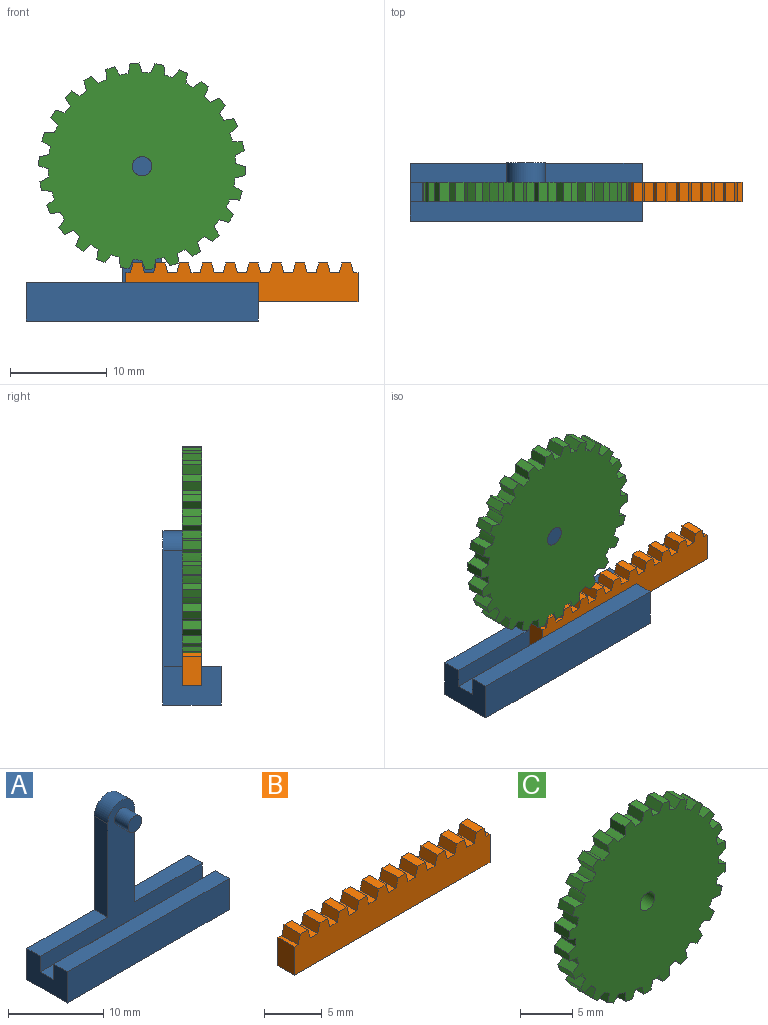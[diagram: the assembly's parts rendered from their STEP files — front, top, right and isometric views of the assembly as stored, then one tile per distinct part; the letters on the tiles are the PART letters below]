
ASSEMBLY  parts=3 mates=2
PART A: 16 faces, bbox 24x6x18 mm
  f0: plane 24x18mm, normal (0,1,0), area 150.3mm2, adj f4,f7,f8,f11,f12,f13,f14,f15
  f1: plane 24x2mm, normal (0,1,0), area 48mm2, adj f2,f6,f7,f8
  f2: plane 24x2mm, normal (0,0,1), area 48mm2, adj f1,f3,f7,f8
  f3: plane 24x4mm, normal (0,-1,0), area 96mm2, adj f2,f4,f7,f8
  f4: plane 24x6mm, normal (0,0,-1), area 144mm2, adj f0,f3,f7,f8
  f5: plane 24x16mm, normal (0,-1,0), area 99.1mm2, adj f6,f7,f8,f9,f11,f12,f13,f14
  f6: plane 24x2mm, normal (0,0,1), area 48mm2, adj f1,f5,f7,f8
  f7: plane 6x4mm, normal (1,0,0), area 20mm2, adj f0,f1,f2,f3,f4,f5,f6,f14
  f8: plane 6x4mm, normal (-1,0,0), area 20mm2, adj f0,f1,f2,f3,f4,f5,f6,f15
  f9: cylinder r=1mm len=2mm, axis (0,1,0), area 12.6mm2, adj f5,f10
  f10: plane 2x2mm, normal (0,-1,0), area 3.1mm2, adj f9
  f11: plane 12x2mm, normal (1,0,0), area 24mm2, adj f0,f5,f12,f14
  f12: cylinder r=2mm len=4mm, axis (0,1,0), area 12.6mm2, adj f0,f5,f11,f13
  f13: plane 12x2mm, normal (-1,0,0), area 24mm2, adj f0,f5,f12,f15
  f14: plane 10x2mm, normal (0,0,1), area 20mm2, adj f0,f5,f7,f11
  f15: plane 10x2mm, normal (0,0,1), area 20mm2, adj f0,f5,f8,f13
PART B: 46 faces, bbox 24x2x4 mm
  f0: plane 3x2mm, normal (1,0,0), area 6mm2, adj f1,f43,f44,f45
  f1: plane 2x0.47mm, normal (0,0,1), area 0.9mm2, adj f0,f2,f44,f45
  f2: plane 2x1mm, normal (0.97,0,0.26), area 2.1mm2, adj f1,f3,f44,f45
  f3: plane 2x0.93mm, normal (0,0,1), area 1.9mm2, adj f2,f4,f44,f45
  f4: plane 2x1mm, normal (-0.97,0,0.26), area 2.1mm2, adj f3,f5,f44,f45
  f5: plane 2x0.93mm, normal (0,0,1), area 1.9mm2, adj f4,f6,f44,f45
  f6: plane 2x1mm, normal (0.97,0,0.26), area 2.1mm2, adj f5,f7,f44,f45
  f7: plane 2x0.93mm, normal (0,0,1), area 1.9mm2, adj f6,f8,f44,f45
  f8: plane 2x1mm, normal (-0.97,0,0.26), area 2.1mm2, adj f7,f9,f44,f45
  f9: plane 2x0.93mm, normal (0,0,1), area 1.9mm2, adj f8,f10,f44,f45
  f10: plane 2x1mm, normal (0.97,0,0.26), area 2.1mm2, adj f9,f11,f44,f45
  f11: plane 2x0.93mm, normal (0,0,1), area 1.9mm2, adj f10,f12,f44,f45
  f12: plane 2x1mm, normal (-0.97,0,0.26), area 2.1mm2, adj f11,f13,f44,f45
  f13: plane 2x0.93mm, normal (0,0,1), area 1.9mm2, adj f12,f14,f44,f45
  f14: plane 2x1mm, normal (0.97,0,0.26), area 2.1mm2, adj f13,f15,f44,f45
  f15: plane 2x0.93mm, normal (0,0,1), area 1.9mm2, adj f14,f16,f44,f45
  f16: plane 2x1mm, normal (-0.97,0,0.26), area 2.1mm2, adj f15,f17,f44,f45
  f17: plane 2x0.93mm, normal (0,0,1), area 1.9mm2, adj f16,f18,f44,f45
  f18: plane 2x1mm, normal (0.97,0,0.26), area 2.1mm2, adj f17,f19,f44,f45
  f19: plane 2x0.93mm, normal (0,0,1), area 1.9mm2, adj f18,f20,f44,f45
  f20: plane 2x1mm, normal (-0.97,0,0.26), area 2.1mm2, adj f19,f21,f44,f45
  f21: plane 2x0.93mm, normal (0,0,1), area 1.9mm2, adj f20,f22,f44,f45
  f22: plane 2x1mm, normal (0.97,0,0.26), area 2.1mm2, adj f21,f23,f44,f45
  f23: plane 2x0.93mm, normal (0,0,1), area 1.9mm2, adj f22,f24,f44,f45
  f24: plane 2x1mm, normal (-0.97,0,0.26), area 2.1mm2, adj f23,f25,f44,f45
  f25: plane 2x0.93mm, normal (0,0,1), area 1.9mm2, adj f24,f26,f44,f45
  f26: plane 2x1mm, normal (0.97,0,0.26), area 2.1mm2, adj f25,f27,f44,f45
  f27: plane 2x0.93mm, normal (0,0,1), area 1.9mm2, adj f26,f28,f44,f45
  f28: plane 2x1mm, normal (-0.97,0,0.26), area 2.1mm2, adj f27,f29,f44,f45
  f29: plane 2x0.93mm, normal (0,0,1), area 1.9mm2, adj f28,f30,f44,f45
  f30: plane 2x1mm, normal (0.97,0,0.26), area 2.1mm2, adj f29,f31,f44,f45
  f31: plane 2x0.93mm, normal (0,0,1), area 1.9mm2, adj f30,f32,f44,f45
  f32: plane 2x1mm, normal (-0.97,0,0.26), area 2.1mm2, adj f31,f33,f44,f45
  f33: plane 2x0.93mm, normal (0,0,1), area 1.9mm2, adj f32,f34,f44,f45
  f34: plane 2x1mm, normal (0.97,0,0.26), area 2.1mm2, adj f33,f35,f44,f45
  f35: plane 2x0.93mm, normal (0,0,1), area 1.9mm2, adj f34,f36,f44,f45
  f36: plane 2x1mm, normal (-0.97,0,0.26), area 2.1mm2, adj f35,f37,f44,f45
  f37: plane 2x0.93mm, normal (0,0,1), area 1.9mm2, adj f36,f38,f44,f45
  f38: plane 2x1mm, normal (0.97,0,0.26), area 2.1mm2, adj f37,f39,f44,f45
  f39: plane 2x0.93mm, normal (0,0,1), area 1.9mm2, adj f38,f40,f44,f45
  f40: plane 2x1mm, normal (-0.97,0,0.26), area 2.1mm2, adj f39,f41,f44,f45
  f41: plane 2x0.47mm, normal (0,0,1), area 0.9mm2, adj f40,f42,f44,f45
  f42: plane 3x2mm, normal (-1,0,0), area 6mm2, adj f41,f43,f44,f45
  f43: plane 24x2mm, normal (0,0,-1), area 48mm2, adj f0,f42,f44,f45
  f44: plane 24x4mm, normal (0,-1,0), area 84mm2, adj f0,f1,f2,f3,f4,f5,f6,f7
  f45: plane 24x4mm, normal (0,1,0), area 84mm2, adj f0,f1,f2,f3,f4,f5,f6,f7
PART C: 107 faces, bbox 21.3x2x21.3 mm
  f0: plane 2x0.86mm, normal (-0.55,0,0.83), area 2.1mm2, adj f1,f103,f105,f106
  f1: cylinder r=9.7mm len=2mm, axis (0,1,0), area 1.7mm2, adj f0,f2,f105,f106
  f2: plane 2x1.01mm, normal (0.98,0,-0.22), area 2.1mm2, adj f1,f3,f105,f106
  f3: plane 2x0.83mm, normal (0.46,0,0.89), area 1.9mm2, adj f2,f4,f105,f106
  f4: plane 2x0.76mm, normal (-0.74,0,0.68), area 2.1mm2, adj f3,f5,f105,f106
  f5: cylinder r=9.7mm len=2mm, axis (0,1,0), area 1.7mm2, adj f4,f6,f105,f106
  f6: plane 2x1.04mm, normal (1,0,0.02), area 2.1mm2, adj f5,f7,f105,f106
  f7: plane 2x0.91mm, normal (0.24,0,0.97), area 1.9mm2, adj f6,f8,f105,f106
  f8: plane 2x0.91mm, normal (-0.88,0,0.48), area 2.1mm2, adj f7,f9,f105,f106
  f9: cylinder r=9.7mm len=2mm, axis (0,1,0), area 1.7mm2, adj f8,f10,f105,f106
  f10: plane 2x1mm, normal (0.97,0,0.26), area 2.1mm2, adj f9,f11,f105,f106
  f11: plane 2x0.93mm, normal (0,0,1), area 1.9mm2, adj f10,f12,f105,f106
  f12: plane 2x1mm, normal (-0.97,0,0.26), area 2.1mm2, adj f11,f13,f105,f106
  f13: cylinder r=9.7mm len=2mm, axis (0,1,0), area 1.7mm2, adj f12,f14,f105,f106
  f14: plane 2x0.91mm, normal (0.88,0,0.48), area 2.1mm2, adj f13,f15,f105,f106
  f15: plane 2x0.91mm, normal (-0.24,0,0.97), area 1.9mm2, adj f14,f16,f105,f106
  f16: plane 2x1.04mm, normal (-1,0,0.02), area 2.1mm2, adj f15,f17,f105,f106
  f17: cylinder r=9.7mm len=2mm, axis (0,1,0), area 1.7mm2, adj f16,f18,f105,f106
  f18: plane 2x0.76mm, normal (0.74,0,0.68), area 2.1mm2, adj f17,f19,f105,f106
  f19: plane 2x0.83mm, normal (-0.46,0,0.89), area 1.9mm2, adj f18,f20,f105,f106
  f20: plane 2x1.01mm, normal (-0.98,0,-0.22), area 2.1mm2, adj f19,f21,f105,f106
  f21: cylinder r=9.7mm len=2mm, axis (0,1,0), area 1.7mm2, adj f20,f22,f105,f106
  f22: plane 2x0.86mm, normal (0.55,0,0.83), area 2.1mm2, adj f21,f23,f105,f106
  f23: plane 2x0.7mm, normal (-0.66,0,0.75), area 1.9mm2, adj f22,f24,f105,f106
  f24: plane 2x0.93mm, normal (-0.89,0,-0.45), area 2.1mm2, adj f23,f25,f105,f106
  f25: cylinder r=9.7mm len=2mm, axis (0,1,0), area 1.7mm2, adj f24,f26,f105,f106
  f26: plane 2x0.98mm, normal (0.34,0,0.94), area 2.1mm2, adj f25,f27,f105,f106
  f27: plane 2x0.77mm, normal (-0.82,0,0.57), area 1.9mm2, adj f26,f28,f105,f106
  f28: plane 2x0.79mm, normal (-0.76,0,-0.65), area 2.1mm2, adj f27,f29,f105,f106
  f29: cylinder r=9.7mm len=2mm, axis (0,1,0), area 1.7mm2, adj f28,f30,f105,f106
  f30: plane 2x1.03mm, normal (0.1,0,0.99), area 2.1mm2, adj f29,f31,f105,f106
  f31: plane 2x0.87mm, normal (-0.94,0,0.35), area 1.9mm2, adj f30,f32,f105,f106
  f32: plane 2x0.84mm, normal (-0.58,0,-0.81), area 2.1mm2, adj f31,f33,f105,f106
  f33: cylinder r=9.7mm len=2mm, axis (0,1,0), area 1.7mm2, adj f32,f34,f105,f106
  f34: plane 2x1.03mm, normal (-0.14,0,0.99), area 2.1mm2, adj f33,f35,f105,f106
  f35: plane 2x0.93mm, normal (-0.99,0,0.12), area 1.9mm2, adj f34,f36,f105,f106
  f36: plane 2x0.96mm, normal (-0.37,0,-0.93), area 2.1mm2, adj f35,f37,f105,f106
  f37: cylinder r=9.7mm len=2mm, axis (0,1,0), area 1.7mm2, adj f36,f38,f105,f106
  f38: plane 2x0.96mm, normal (-0.37,0,0.93), area 2.1mm2, adj f37,f39,f105,f106
  f39: plane 2x0.93mm, normal (-0.99,0,-0.12), area 1.9mm2, adj f38,f40,f105,f106
  f40: plane 2x1.03mm, normal (-0.14,0,-0.99), area 2.1mm2, adj f39,f41,f105,f106
  f41: cylinder r=9.7mm len=2mm, axis (0,1,0), area 1.7mm2, adj f40,f42,f105,f106
  f42: plane 2x0.84mm, normal (-0.58,0,0.81), area 2.1mm2, adj f41,f43,f105,f106
  f43: plane 2x0.87mm, normal (-0.94,0,-0.35), area 1.9mm2, adj f42,f44,f105,f106
  f44: plane 2x1.03mm, normal (0.1,0,-0.99), area 2.1mm2, adj f43,f45,f105,f106
  f45: cylinder r=9.7mm len=2mm, axis (0,1,0), area 1.7mm2, adj f44,f46,f105,f106
  f46: plane 2x0.79mm, normal (-0.76,0,0.65), area 2.1mm2, adj f45,f47,f105,f106
  f47: plane 2x0.77mm, normal (-0.82,0,-0.57), area 1.9mm2, adj f46,f48,f105,f106
  f48: plane 2x0.98mm, normal (0.34,0,-0.94), area 2.1mm2, adj f47,f49,f105,f106
  f49: cylinder r=9.7mm len=2mm, axis (0,1,0), area 1.7mm2, adj f48,f50,f105,f106
  f50: plane 2x0.93mm, normal (-0.89,0,0.45), area 2.1mm2, adj f49,f51,f105,f106
  f51: plane 2x0.7mm, normal (-0.66,0,-0.75), area 1.9mm2, adj f50,f52,f105,f106
  f52: plane 2x0.86mm, normal (0.55,0,-0.83), area 2.1mm2, adj f51,f53,f105,f106
  f53: cylinder r=9.7mm len=2mm, axis (0,1,0), area 1.7mm2, adj f52,f54,f105,f106
  f54: plane 2x1.01mm, normal (-0.98,0,0.22), area 2.1mm2, adj f53,f55,f105,f106
  f55: plane 2x0.83mm, normal (-0.46,0,-0.89), area 1.9mm2, adj f54,f56,f105,f106
  f56: plane 2x0.76mm, normal (0.74,0,-0.68), area 2.1mm2, adj f55,f57,f105,f106
  f57: cylinder r=9.7mm len=2mm, axis (0,1,0), area 1.7mm2, adj f56,f58,f105,f106
  f58: plane 2x1.04mm, normal (-1,0,-0.02), area 2.1mm2, adj f57,f59,f105,f106
  f59: plane 2x0.91mm, normal (-0.24,0,-0.97), area 1.9mm2, adj f58,f60,f105,f106
  f60: plane 2x0.91mm, normal (0.88,0,-0.48), area 2.1mm2, adj f59,f61,f105,f106
  f61: cylinder r=9.7mm len=2mm, axis (0,1,0), area 1.7mm2, adj f60,f62,f105,f106
  f62: plane 2x1mm, normal (-0.97,0,-0.26), area 2.1mm2, adj f61,f63,f105,f106
  f63: plane 2x0.93mm, normal (0,0,-1), area 1.9mm2, adj f62,f64,f105,f106
  f64: plane 2x1mm, normal (0.97,0,-0.26), area 2.1mm2, adj f63,f65,f105,f106
  f65: cylinder r=9.7mm len=2mm, axis (0,1,0), area 1.7mm2, adj f64,f66,f105,f106
  f66: plane 2x0.91mm, normal (-0.88,0,-0.48), area 2.1mm2, adj f65,f67,f105,f106
  f67: plane 2x0.91mm, normal (0.24,0,-0.97), area 1.9mm2, adj f66,f68,f105,f106
  f68: plane 2x1.04mm, normal (1,0,-0.02), area 2.1mm2, adj f67,f69,f105,f106
  f69: cylinder r=9.7mm len=2mm, axis (0,1,0), area 1.7mm2, adj f68,f70,f105,f106
  f70: plane 2x0.76mm, normal (-0.74,0,-0.68), area 2.1mm2, adj f69,f71,f105,f106
  f71: plane 2x0.83mm, normal (0.46,0,-0.89), area 1.9mm2, adj f70,f72,f105,f106
  f72: plane 2x1.01mm, normal (0.98,0,0.22), area 2.1mm2, adj f71,f73,f105,f106
  f73: cylinder r=9.7mm len=2mm, axis (0,1,0), area 1.7mm2, adj f72,f74,f105,f106
  f74: plane 2x0.86mm, normal (-0.55,0,-0.83), area 2.1mm2, adj f73,f75,f105,f106
  f75: plane 2x0.7mm, normal (0.66,0,-0.75), area 1.9mm2, adj f74,f76,f105,f106
  f76: plane 2x0.93mm, normal (0.89,0,0.45), area 2.1mm2, adj f75,f77,f105,f106
  f77: cylinder r=9.7mm len=2mm, axis (0,1,0), area 1.7mm2, adj f76,f78,f105,f106
  f78: plane 2x0.98mm, normal (-0.34,0,-0.94), area 2.1mm2, adj f77,f79,f105,f106
  f79: plane 2x0.77mm, normal (0.82,0,-0.57), area 1.9mm2, adj f78,f80,f105,f106
  f80: plane 2x0.79mm, normal (0.76,0,0.65), area 2.1mm2, adj f79,f81,f105,f106
  f81: cylinder r=9.7mm len=2mm, axis (0,1,0), area 1.7mm2, adj f80,f82,f105,f106
  f82: plane 2x1.03mm, normal (-0.1,0,-0.99), area 2.1mm2, adj f81,f83,f105,f106
  f83: plane 2x0.87mm, normal (0.94,0,-0.35), area 1.9mm2, adj f82,f84,f105,f106
  f84: plane 2x0.84mm, normal (0.58,0,0.81), area 2.1mm2, adj f83,f85,f105,f106
  f85: cylinder r=9.7mm len=2mm, axis (0,1,0), area 1.7mm2, adj f84,f86,f105,f106
  f86: plane 2x1.03mm, normal (0.14,0,-0.99), area 2.1mm2, adj f85,f87,f105,f106
  f87: plane 2x0.93mm, normal (0.99,0,-0.12), area 1.9mm2, adj f86,f88,f105,f106
  f88: plane 2x0.96mm, normal (0.37,0,0.93), area 2.1mm2, adj f87,f89,f105,f106
  f89: cylinder r=9.7mm len=2mm, axis (0,1,0), area 1.7mm2, adj f88,f90,f105,f106
  f90: plane 2x0.96mm, normal (0.37,0,-0.93), area 2.1mm2, adj f89,f91,f105,f106
  f91: plane 2x0.93mm, normal (0.99,0,0.12), area 1.9mm2, adj f90,f92,f105,f106
  f92: plane 2x1.03mm, normal (0.14,0,0.99), area 2.1mm2, adj f91,f93,f105,f106
  f93: cylinder r=9.7mm len=2mm, axis (0,1,0), area 1.7mm2, adj f92,f94,f105,f106
  f94: plane 2x0.84mm, normal (0.58,0,-0.81), area 2.1mm2, adj f93,f95,f105,f106
  f95: plane 2x0.87mm, normal (0.94,0,0.35), area 1.9mm2, adj f94,f96,f105,f106
  f96: plane 2x1.03mm, normal (-0.1,0,0.99), area 2.1mm2, adj f95,f97,f105,f106
  f97: cylinder r=9.7mm len=2mm, axis (0,1,0), area 1.7mm2, adj f96,f98,f105,f106
  f98: plane 2x0.79mm, normal (0.76,0,-0.65), area 2.1mm2, adj f97,f99,f105,f106
  f99: plane 2x0.77mm, normal (0.82,0,0.57), area 1.9mm2, adj f98,f100,f105,f106
  f100: plane 2x0.98mm, normal (-0.34,0,0.94), area 2.1mm2, adj f99,f101,f105,f106
  f101: cylinder r=9.7mm len=2mm, axis (0,1,0), area 1.7mm2, adj f100,f102,f105,f106
  f102: plane 2x0.93mm, normal (0.89,0,-0.45), area 2.1mm2, adj f101,f103,f105,f106
  f103: plane 2x0.7mm, normal (0.66,0,0.75), area 1.9mm2, adj f0,f102,f105,f106
  f104: cylinder r=1mm len=2mm, axis (0,1,0), area 12.6mm2, adj f105,f106
  f105: plane 21.34x21.3mm, normal (0,-1,0), area 322.9mm2, adj f0,f1,f2,f3,f4,f5,f6,f7
  f106: plane 21.34x21.3mm, normal (0,1,0), area 322.9mm2, adj f0,f1,f2,f3,f4,f5,f6,f7
PLACE A at identity fixed
PLACE B t=(10.32,0,0)mm
PLACE C rot(axis=(0,-1,0),59.6deg) t=(12.07,0,6.91)mm
MATE revolute A.f9 <-> C.f104  axis (0,-1,0) through (0,0,14)mm
MATE slider B.f0 <-> A.f7  axis (1,0,0) through (22.32,1,0)mm
